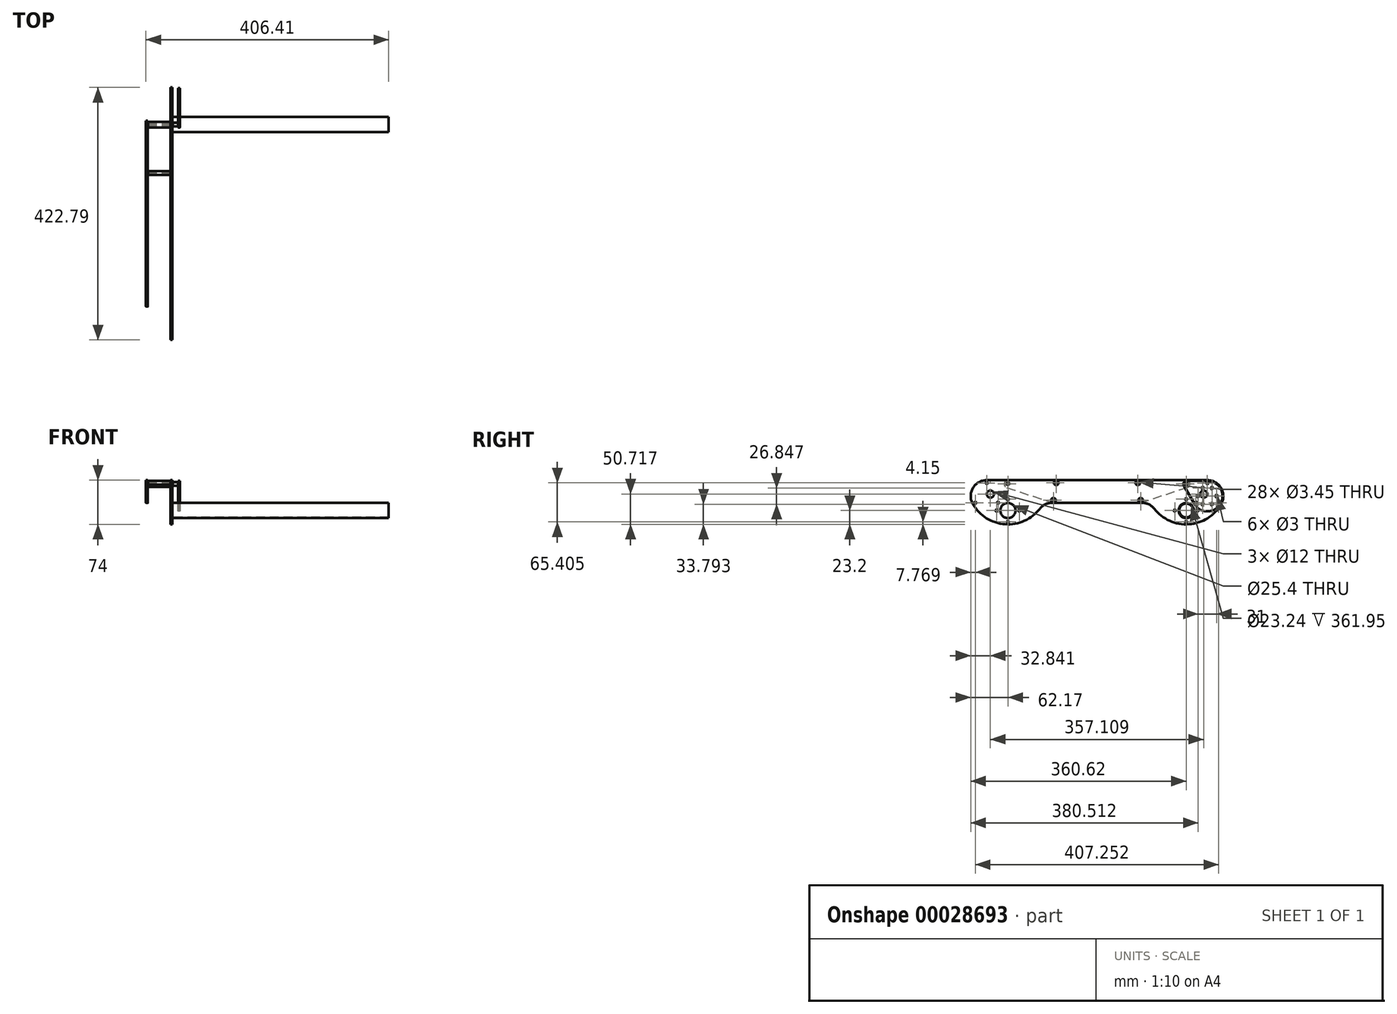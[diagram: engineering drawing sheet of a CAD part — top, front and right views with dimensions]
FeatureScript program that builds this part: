
annotation { "Feature Type Name" : "Feature", "Feature Type Description" : "" }
export const myFeature = defineFeature(function(context is Context, id is Id, definition is map)
    precondition{}
    {
        {
            var Q0;
            Q0=qCreatedBy(makeId("Right.planeOp"),FACE);
            var sketch = newSketch(context, id + "F0", { "sketchPlane" : qUnion([Q0])});
            skCircle(sketch, "E0", {"center": v(0, 0) * mm, "radius": 76.2 * mm});
            skLineSegment(sketch, "E1", {"start": v(79.37, -76.2) * mm, "end": v(-377.83, -76.2) * mm, "construction": true});
            skLineSegment(sketch, "E2", {"start": v(-229.18, -31.75) * mm, "end": v(-69.27, -31.75) * mm});
            skCircle(sketch, "E3.cCircle", {"center": v(-94.33, -49.53) * mm, "radius": 6.35 * mm, "construction": true});
            skLineSegment(sketch, "E3.0", {"start": v(-90.67, -43.18) * mm, "end": v(-87, -49.53) * mm});
            skLineSegment(sketch, "E3.1", {"start": v(-87, -49.53) * mm, "end": v(-90.67, -55.88) * mm});
            skLineSegment(sketch, "E3.2", {"start": v(-90.67, -55.88) * mm, "end": v(-98, -55.88) * mm});
            skLineSegment(sketch, "E3.3", {"start": v(-98, -55.88) * mm, "end": v(-101.67, -49.53) * mm});
            skLineSegment(sketch, "E3.4", {"start": v(-101.67, -49.53) * mm, "end": v(-98, -43.18) * mm});
            skLineSegment(sketch, "E3.5", {"start": v(-98, -43.18) * mm, "end": v(-90.67, -43.18) * mm});
            skPoint(sketch, "E3.0.midPoint", {"position": v(-88.84, -46.35) * mm});
            skLineSegment(sketch, "E4", {"start": v(79.37, -76.2) * mm, "end": v(79.37, 381) * mm, "construction": true});
            skLineSegment(sketch, "E5", {"start": v(79.38, 381) * mm, "end": v(-377.83, 381) * mm, "construction": true});
            skLineSegment(sketch, "E6", {"start": v(-377.83, 381) * mm, "end": v(-377.83, -76.2) * mm, "construction": true});
            skCircle(sketch, "E7", {"center": v(-298.45, 0) * mm, "radius": 76.2 * mm});
            skLineSegment(sketch, "E8", {"start": v(-149.23, -76.2) * mm, "end": v(-149.23, 381) * mm, "construction": true});
            skLineSegment(sketch, "E9", {"start": v(-75.93, 6.35) * mm, "end": v(-222.52, 6.35) * mm});
            skCircle(sketch, "E10", {"center": v(0, 0) * mm, "radius": 50.8 * mm, "construction": true});
            skCircle(sketch, "E11", {"center": v(29.33, -16.93) * mm, "radius": 16.93 * mm, "construction": true});
            skLineSegment(sketch, "E12", {"start": v(0, 0) * mm, "end": v(0, -50.8) * mm, "construction": true});
            skLineSegment(sketch, "E13", {"start": v(0, 0) * mm, "end": v(29.33, -16.93) * mm, "construction": true});
            skCircle(sketch, "E14", {"center": v(0, 0) * mm, "radius": 4.76 * mm, "construction": true});
            skCircle(sketch, "E15", {"center": v(0, -44.45) * mm, "radius": 12.7 * mm});
            skLineSegment(sketch, "E16.rect.bottom", {"start": v(-2.03, -65.53) * mm, "end": v(-21.08, -46.48) * mm});
            skLineSegment(sketch, "E16.rect.top", {"start": v(21.08, -42.42) * mm, "end": v(2.03, -23.37) * mm});
            skLineSegment(sketch, "E16.rect.left", {"start": v(2.03, -65.53) * mm, "end": v(21.08, -46.48) * mm});
            skLineSegment(sketch, "E16.rect.right", {"start": v(-21.08, -42.42) * mm, "end": v(-2.03, -23.37) * mm});
            skPoint(sketch, "E17.visualSharp", {"position": v(23.1, -44.45) * mm});
            skArc(sketch, "E17.filletArc", {"start": v(21.08, -46.48) * mm, "mid": v(21.92, -44.45) * mm, "end": v(21.08, -42.42) * mm});
            skPoint(sketch, "E18.visualSharp", {"position": v(0, -67.56) * mm});
            skArc(sketch, "E18.filletArc", {"start": v(-2.03, -65.53) * mm, "mid": v(0, -66.37) * mm, "end": v(2.03, -65.53) * mm});
            skPoint(sketch, "E19.visualSharp", {"position": v(-23.1, -44.45) * mm});
            skArc(sketch, "E19.filletArc", {"start": v(-21.08, -42.42) * mm, "mid": v(-21.92, -44.45) * mm, "end": v(-21.08, -46.48) * mm});
            skPoint(sketch, "E20.visualSharp", {"position": v(0, -21.34) * mm});
            skArc(sketch, "E20.filletArc", {"start": v(2.03, -23.37) * mm, "mid": v(0, -22.53) * mm, "end": v(-2.03, -23.37) * mm});
            skLineSegment(sketch, "E21", {"start": v(0, 0) * mm, "end": v(0, -44.45) * mm});
            skCircle(sketch, "E22.MirrorC", {"center": v(-298.45, -44.45) * mm, "radius": 12.7 * mm});
            skArc(sketch, "E23.MirrorCS", {"start": v(-300.48, -23.37) * mm, "mid": v(-298.45, -22.53) * mm, "end": v(-296.42, -23.37) * mm});
            skArc(sketch, "E24.MirrorCS", {"start": v(-319.53, -46.48) * mm, "mid": v(-320.37, -44.45) * mm, "end": v(-319.53, -42.42) * mm});
            skLineSegment(sketch, "E25.MirrorCS", {"start": v(-319.53, -42.42) * mm, "end": v(-300.48, -23.37) * mm});
            skLineSegment(sketch, "E26.MirrorCS", {"start": v(-300.48, -65.53) * mm, "end": v(-319.53, -46.48) * mm});
            skArc(sketch, "E27.MirrorCS", {"start": v(-296.42, -65.53) * mm, "mid": v(-298.45, -66.37) * mm, "end": v(-300.48, -65.53) * mm});
            skLineSegment(sketch, "E28.MirrorCS", {"start": v(-277.37, -42.42) * mm, "end": v(-296.42, -23.37) * mm});
            skLineSegment(sketch, "E29.MirrorCS", {"start": v(-296.42, -65.53) * mm, "end": v(-277.37, -46.48) * mm});
            skArc(sketch, "E30.MirrorCS", {"start": v(-277.37, -42.42) * mm, "mid": v(-276.53, -44.45) * mm, "end": v(-277.37, -46.48) * mm});
            skCircle(sketch, "E31", {"center": v(0, -44.45) * mm, "radius": 19.05 * mm});
            skCircle(sketch, "E32", {"center": v(0, -44.45) * mm, "radius": 11.62 * mm});
            skCircle(sketch, "E33", {"center": v(0, -44.45) * mm, "radius": 26.92 * mm, "construction": true});
            skSolve(sketch);
        }
        {
            var Q0;
            Q0=qCreatedBy(makeId("Right.planeOp"),FACE);
            var sketch = newSketch(context, id + "F1", { "sketchPlane" : qUnion([Q0])});
            skArc(sketch, "E34", {"start": v(-59.74, -31.75) * mm, "mid": v(-1.19, -67.64) * mm, "end": v(58.59, -33.83) * mm});
            skArc(sketch, "E35", {"start": v(-357.04, -33.83) * mm, "mid": v(-297.26, -67.64) * mm, "end": v(-238.71, -31.75) * mm});
            skLineSegment(sketch, "E36", {"start": v(-333.84, 6.35) * mm, "end": v(35.4, 6.35) * mm});
            skLineSegment(sketch, "E37", {"start": v(-59.74, -31.75) * mm, "end": v(-238.71, -31.75) * mm});
            skCircle(sketch, "E38", {"center": v(0, 0) * mm, "radius": 1.73 * mm});
            skCircle(sketch, "E39", {"center": v(-298.45, 0) * mm, "radius": 1.73 * mm});
            skCircle(sketch, "E40", {"center": v(29.33, -16.93) * mm, "radius": 6 * mm});
            skCircle(sketch, "E41.MirrorC", {"center": v(-327.78, -16.93) * mm, "radius": 6 * mm});
            skArc(sketch, "E42", {"start": v(58.59, -33.82) * mm, "mid": v(58.59, -7.04) * mm, "end": v(35.4, 6.35) * mm});
            skPoint(sketch, "E43.orphan", {"position": v(67.35, 6.35) * mm});
            skArc(sketch, "E44.MirrorCS", {"start": v(-357.04, -33.83) * mm, "mid": v(-357.04, -7.04) * mm, "end": v(-333.84, 6.35) * mm});
            skPoint(sketch, "E45.orphan", {"position": v(-365.8, 6.35) * mm});
            skCircle(sketch, "E46.0", {"center": v(-298.45, -44.45) * mm, "radius": 12.7 * mm});
            skCircle(sketch, "E46.1", {"center": v(0, -44.45) * mm, "radius": 12.7 * mm});
            skSolve(sketch);
        }
        {
            var Q0;
            Q0 = qSketchRegion(id + "F1", true);
            var Q1;
            Q1=makeQuery(id+"F1.imprint","IMPRINT",FACE,{"disambiguationData":[TD([[makeQuery(id+"F1.imprint","IMPRINT",EDGE,{"derivedFrom":sQuery(id+"F1.wireOp",EDGE,"E46.0")}),-1.0]])]});
            var Q2;
            Q2=makeQuery(id+"F1.imprint","IMPRINT",FACE,{"disambiguationData":[TD([[makeQuery(id+"F1.imprint","IMPRINT",EDGE,{"derivedFrom":sQuery(id+"F1.wireOp",EDGE,"E46.1")}),1.0]])]});
            extrude(context, id + "F2", {"entities" : qUnion([Q0, Q1, Q2]), "depth" : 3.17 * mm});
        }
        {
            var Q0;
            Q0=makeQuery(id+"F2.opExtrude","CAP_FACE",FACE,{"disambiguationData":[OSD([sQuery(id+"F1.wireOp",EDGE,"E34"),sQuery(id+"F1.wireOp",EDGE,"E35"),sQuery(id+"F1.wireOp",EDGE,"E36"),sQuery(id+"F1.wireOp",EDGE,"E37"),sQuery(id+"F1.wireOp",EDGE,"E38"),sQuery(id+"F1.wireOp",EDGE,"E39"),sQuery(id+"F1.wireOp",EDGE,"E40"),sQuery(id+"F1.wireOp",EDGE,"E41.MirrorC")])],"isStart":false});
            cPlane(context, id + "F3", {"entities" : qUnion([Q0]), "cplaneType" : CPlaneType.OFFSET, "offset" : 9.52 * mm, "width" : 152.4 * mm, "height" : 152.4 * mm});
        }
        {
            var Q0;
            Q0=qCreatedBy(id+"F3.planeOp",FACE);
            var sketch = newSketch(context, id + "F4", { "sketchPlane" : qUnion([Q0])});
            skCircle(sketch, "E47.0", {"center": v(29.33, -16.93) * mm, "radius": 6 * mm});
            skCircle(sketch, "E48", {"center": v(35.4, -20.43) * mm, "radius": 18.5 * mm, "construction": true});
            skCircle(sketch, "E49.cCircle", {"center": v(35.4, -20.43) * mm, "radius": 15.5 * mm, "construction": true});
            skLineSegment(sketch, "E49.0", {"start": v(27.64, -33.86) * mm, "end": v(19.9, -20.43) * mm, "construction": true});
            skLineSegment(sketch, "E49.1", {"start": v(19.9, -20.43) * mm, "end": v(27.64, -7) * mm, "construction": true});
            skLineSegment(sketch, "E49.2", {"start": v(27.64, -7) * mm, "end": v(43.14, -7) * mm, "construction": true});
            skLineSegment(sketch, "E49.3", {"start": v(43.14, -7) * mm, "end": v(50.9, -20.43) * mm, "construction": true});
            skLineSegment(sketch, "E49.4", {"start": v(50.9, -20.43) * mm, "end": v(43.14, -33.86) * mm, "construction": true});
            skLineSegment(sketch, "E49.5", {"start": v(43.14, -33.86) * mm, "end": v(27.64, -33.86) * mm, "construction": true});
            skArc(sketch, "E50.0", {"start": v(-0.03, 4.76) * mm, "mid": v(-4.12, 2.38) * mm, "end": v(-4.14, -2.36) * mm});
            skArc(sketch, "E51", {"start": v(13.32, -33) * mm, "mid": v(57.39, -33.13) * mm, "end": v(35.24, 4.97) * mm});
            skLineSegment(sketch, "E52", {"start": v(-0.03, 4.76) * mm, "end": v(35.24, 4.97) * mm});
            skLineSegment(sketch, "E53", {"start": v(13.32, -33) * mm, "end": v(-4.14, -2.36) * mm});
            skCircle(sketch, "E54.cCircle", {"center": v(35.4, -20.43) * mm, "radius": 21.95 * mm, "construction": true});
            skLineSegment(sketch, "E54.0", {"start": v(35.4, 1.52) * mm, "end": v(54.4, -31.4) * mm, "construction": true});
            skLineSegment(sketch, "E54.1", {"start": v(54.4, -31.4) * mm, "end": v(16.38, -31.4) * mm, "construction": true});
            skLineSegment(sketch, "E54.2", {"start": v(16.38, -31.4) * mm, "end": v(35.4, 1.52) * mm, "construction": true});
            skCircle(sketch, "E55", {"center": v(54.4, -31.4) * mm, "radius": 2.87 * mm, "construction": true});
            skLineSegment(sketch, "E56", {"start": v(51.41, -29.68) * mm, "end": v(57.39, -33.13) * mm, "construction": true});
            skCircle(sketch, "E57.0", {"center": v(0, 0) * mm, "radius": 1.73 * mm});
            skCircle(sketch, "E58", {"center": v(35.4, 1.52) * mm, "radius": 1.73 * mm});
            skCircle(sketch, "E59", {"center": v(16.38, -31.4) * mm, "radius": 1.73 * mm});
            skCircle(sketch, "E60", {"center": v(54.4, -31.4) * mm, "radius": 1.73 * mm});
            skCircle(sketch, "E61.MirrorC", {"center": v(-352.85, -31.4) * mm, "radius": 1.73 * mm, "construction": true});
            skCircle(sketch, "E62.MirrorC", {"center": v(-333.84, 1.52) * mm, "radius": 1.73 * mm, "construction": true});
            skCircle(sketch, "E63.MirrorC", {"center": v(-314.83, -31.4) * mm, "radius": 1.73 * mm, "construction": true});
            skSolve(sketch);
        }
        {
            var Q0;
            Q0 = qSketchRegion(id + "F4", true);
            extrude(context, id + "F5", {"entities" : qUnion([Q0]), "depth" : 3.17 * mm});
        }
        {
            var Q0;
            Q0=sQuery(id+"F4.wireOp",VERTEX,"E49.2.start");
            var Q1;
            Q1=sQuery(id+"F4.wireOp",VERTEX,"E49.1.start");
            var Q2;
            Q2=sQuery(id+"F4.wireOp",VERTEX,"E49.5.end");
            var Q3;
            Q3=sQuery(id+"F4.wireOp",VERTEX,"E49.5.start");
            var Q4;
            Q4=sQuery(id+"F4.wireOp",VERTEX,"E49.4.start");
            var Q5;
            Q5=sQuery(id+"F4.wireOp",VERTEX,"E49.3.start");
            var Q6;
            Q6=makeQuery(id+"F5.opExtrude","SWEPT_BODY",BODY,{"disambiguationData":[OSD([sQuery(id+"F4.wireOp",EDGE,"E47.0"),sQuery(id+"F4.wireOp",EDGE,"E50.0"),sQuery(id+"F4.wireOp",EDGE,"E51"),sQuery(id+"F4.wireOp",EDGE,"E52"),sQuery(id+"F4.wireOp",EDGE,"E53"),sQuery(id+"F4.wireOp",EDGE,"E57.0"),sQuery(id+"F4.wireOp",EDGE,"E58"),sQuery(id+"F4.wireOp",EDGE,"E59"),sQuery(id+"F4.wireOp",EDGE,"E60")])]});
            hole(context, id + "F6", {"style" : HoleStyle.C_SINK, "holeDiameter" : 3 * mm, "cSinkDiameter" : 6 * mm, "endStyle" : HoleEndStyle.THROUGH, "oppositeDirection" : true, "locations" : qUnion([Q0, Q1, Q2, Q3, Q4, Q5]), "scope" : qUnion([Q6]), "cSinkAngle" : 90 * degree});
        }
        {
            var Q0;
            Q0=sQuery(id+"F4.wireOp",VERTEX,"E54.0.end");
            var Q1;
            Q1=sQuery(id+"F4.wireOp",VERTEX,"E54.2.start");
            var Q2;
            Q2=sQuery(id+"F4.wireOp",VERTEX,"E54.2.end");
            var Q3;
            Q3=sQuery(id+"F4.wireOp",VERTEX,"E62.MirrorC.center");
            var Q4;
            Q4=sQuery(id+"F4.wireOp",VERTEX,"E63.MirrorC.center");
            var Q5;
            Q5=sQuery(id+"F4.wireOp",VERTEX,"E61.MirrorC.center");
            var Q6;
            Q6=makeQuery(id+"F2.opExtrude","SWEPT_BODY",BODY,{"disambiguationData":[OSD([sQuery(id+"F1.wireOp",EDGE,"E34"),sQuery(id+"F1.wireOp",EDGE,"E35"),sQuery(id+"F1.wireOp",EDGE,"E36"),sQuery(id+"F1.wireOp",EDGE,"E37"),sQuery(id+"F1.wireOp",EDGE,"E38"),sQuery(id+"F1.wireOp",EDGE,"E39"),sQuery(id+"F1.wireOp",EDGE,"E40"),sQuery(id+"F1.wireOp",EDGE,"E41.MirrorC")])]});
            hole(context, id + "F7", {"style" : HoleStyle.SIMPLE, "holeDiameter" : 3.45 * mm, "endStyle" : HoleEndStyle.THROUGH, "locations" : qUnion([Q0, Q1, Q2, Q3, Q4, Q5]), "scope" : qUnion([Q6])});
        }
        {
            var Q0;
            Q0=sQuery(id+"F0.wireOp",VERTEX,"E20.filletArc.center");
            var Q1;
            Q1=sQuery(id+"F0.wireOp",VERTEX,"E17.filletArc.center");
            var Q2;
            Q2=sQuery(id+"F0.wireOp",VERTEX,"E18.filletArc.center");
            var Q3;
            Q3=sQuery(id+"F0.wireOp",VERTEX,"E19.filletArc.center");
            var Q4;
            Q4=sQuery(id+"F0.wireOp",VERTEX,"E23.MirrorCS.center");
            var Q5;
            Q5=sQuery(id+"F0.wireOp",VERTEX,"E30.MirrorCS.center");
            var Q6;
            Q6=sQuery(id+"F0.wireOp",VERTEX,"E27.MirrorCS.center");
            var Q7;
            Q7=sQuery(id+"F0.wireOp",VERTEX,"E24.MirrorCS.center");
            var Q8;
            Q8=makeQuery(id+"F2.opExtrude","SWEPT_BODY",BODY,{"disambiguationData":[OSD([sQuery(id+"F1.wireOp",EDGE,"E34"),sQuery(id+"F1.wireOp",EDGE,"E35"),sQuery(id+"F1.wireOp",EDGE,"E36"),sQuery(id+"F1.wireOp",EDGE,"E37"),sQuery(id+"F1.wireOp",EDGE,"E38"),sQuery(id+"F1.wireOp",EDGE,"E39"),sQuery(id+"F1.wireOp",EDGE,"E40"),sQuery(id+"F1.wireOp",EDGE,"E41.MirrorC")])]});
            hole(context, id + "F8", {"style" : HoleStyle.SIMPLE, "holeDiameter" : 3.45 * mm, "endStyle" : HoleEndStyle.THROUGH, "oppositeDirection" : true, "locations" : qUnion([Q0, Q1, Q2, Q3, Q4, Q5, Q6, Q7]), "scope" : qUnion([Q8])});
        }
        {
            var Q0;
            Q0=makeQuery(id+"F2.opExtrude","SWEPT_EDGE",EDGE,{"disambiguationData":[OSD([sQuery(id+"F1.wireOp",EDGE,"E35"),sQuery(id+"F1.wireOp",EDGE,"E37")])]});
            var Q1;
            Q1=makeQuery(id+"F2.opExtrude","SWEPT_EDGE",EDGE,{"disambiguationData":[OSD([sQuery(id+"F1.wireOp",EDGE,"E34"),sQuery(id+"F1.wireOp",EDGE,"E37")])]});
            fillet(context, id + "F9", {"entities" : qUnion([Q0, Q1]), "radius" : 25.4 * mm, "tangentPropagation" : true, "allowEdgeOverflow" : false});
        }
        {
            var Q0;
            Q0=makeQuery(id+"F2.opExtrude","CAP_FACE",FACE,{"disambiguationData":[OSD([sQuery(id+"F1.wireOp",EDGE,"E34"),sQuery(id+"F1.wireOp",EDGE,"E35"),sQuery(id+"F1.wireOp",EDGE,"E36"),sQuery(id+"F1.wireOp",EDGE,"E37"),sQuery(id+"F1.wireOp",EDGE,"E38"),sQuery(id+"F1.wireOp",EDGE,"E39"),sQuery(id+"F1.wireOp",EDGE,"E40"),sQuery(id+"F1.wireOp",EDGE,"E41.MirrorC"),sQuery(id+"F1.wireOp",EDGE,"E42"),sQuery(id+"F1.wireOp",EDGE,"E44.MirrorCS"),sQuery(id+"F1.wireOp",EDGE,"E46.0"),sQuery(id+"F1.wireOp",EDGE,"E46.1")])],"isStart":false});
            var sketch = newSketch(context, id + "F10", { "sketchPlane" : qUnion([Q0])});
            skCircle(sketch, "E64", {"center": v(0, 0) * mm, "radius": 80.96 * mm, "construction": true});
            skCircle(sketch, "E65", {"center": v(-80.94, 1.9) * mm, "radius": 4.45 * mm, "construction": true});
            skCircle(sketch, "E66", {"center": v(-80.94, 1.9) * mm, "radius": 1.7 * mm});
            skCircle(sketch, "E67", {"center": v(-76.22, -27.3) * mm, "radius": 4.45 * mm, "construction": true});
            skCircle(sketch, "E68", {"center": v(-76.22, -27.3) * mm, "radius": 1.7 * mm});
            skCircle(sketch, "E69.MirrorC", {"center": v(-217.5, 1.9) * mm, "radius": 1.7 * mm});
            skCircle(sketch, "E70.MirrorC", {"center": v(-222.23, -27.3) * mm, "radius": 1.7 * mm});
            skSolve(sketch);
        }
        {
            var Q0;
            Q0=makeQuery(id+"F1.imprint","IMPRINT",FACE,{"disambiguationData":[TD([[makeQuery(id+"F1.imprint","IMPRINT",EDGE,{"derivedFrom":sQuery(id+"F1.wireOp",EDGE,"E34")}),1.0]])]});
            cPlane(context, id + "F11", {"entities" : qUnion([Q0]), "cplaneType" : CPlaneType.OFFSET, "offset" : 38.1 * mm, "oppositeDirection" : true, "width" : 152.4 * mm, "height" : 152.4 * mm});
        }
        {
            var Q0;
            Q0=qCreatedBy(id+"F11.planeOp",FACE);
            var sketch = newSketch(context, id + "F12", { "sketchPlane" : qUnion([Q0])});
            skLineSegment(sketch, "E71.0", {"start": v(-298.45, 6.35) * mm, "end": v(0, 6.35) * mm});
            skLineSegment(sketch, "E71.1", {"start": v(-77.55, -31.75) * mm, "end": v(-220.9, -31.75) * mm});
            skArc(sketch, "E72", {"start": v(2, -6.03) * mm, "mid": v(6.27, 1.01) * mm, "end": v(0, 6.35) * mm});
            skArc(sketch, "E73", {"start": v(-298.45, 6.35) * mm, "mid": v(-304.72, 1.01) * mm, "end": v(-300.45, -6.03) * mm});
            skPoint(sketch, "E74.orphan", {"position": v(35.4, 6.35) * mm});
            skPoint(sketch, "E75.orphan", {"position": v(-333.84, 6.35) * mm});
            skLineSegment(sketch, "E76", {"start": v(-300.45, -6.03) * mm, "end": v(-224.9, -31.1) * mm});
            skLineSegment(sketch, "E77", {"start": v(2, -6.03) * mm, "end": v(-73.55, -31.1) * mm});
            skCircle(sketch, "E78.0", {"center": v(0, 0) * mm, "radius": 1.73 * mm});
            skCircle(sketch, "E79.1", {"center": v(-298.45, 0) * mm, "radius": 1.73 * mm});
            skLineSegment(sketch, "E80", {"start": v(-149.23, 6.35) * mm, "end": v(-149.23, -31.75) * mm, "construction": true});
            skPoint(sketch, "E81.visualSharp", {"position": v(-75.5, -31.75) * mm});
            skArc(sketch, "E81.filletArc", {"start": v(-77.55, -31.75) * mm, "mid": v(-75.53, -31.59) * mm, "end": v(-73.55, -31.1) * mm});
            skPoint(sketch, "E82.visualSharp", {"position": v(-222.95, -31.75) * mm});
            skArc(sketch, "E82.filletArc", {"start": v(-224.9, -31.1) * mm, "mid": v(-222.92, -31.59) * mm, "end": v(-220.9, -31.75) * mm});
            skSolve(sketch);
        }
        {
            var Q0;
            Q0 = qSketchRegion(id + "F12", true);
            extrude(context, id + "F13", {"entities" : qUnion([Q0]), "oppositeDirection" : true, "depth" : 3.17 * mm});
        }
        {
            var Q0;
            Q0=makeQuery(id+"F2.opExtrude","CAP_FACE",FACE,{"disambiguationData":[OSD([sQuery(id+"F1.wireOp",EDGE,"E34"),sQuery(id+"F1.wireOp",EDGE,"E35"),sQuery(id+"F1.wireOp",EDGE,"E36"),sQuery(id+"F1.wireOp",EDGE,"E37"),sQuery(id+"F1.wireOp",EDGE,"E38"),sQuery(id+"F1.wireOp",EDGE,"E39"),sQuery(id+"F1.wireOp",EDGE,"E40"),sQuery(id+"F1.wireOp",EDGE,"E41.MirrorC"),sQuery(id+"F1.wireOp",EDGE,"E42"),sQuery(id+"F1.wireOp",EDGE,"E44.MirrorCS")])],"isStart":true});
            var sketch = newSketch(context, id + "F14", { "sketchPlane" : qUnion([Q0])});
            skCircle(sketch, "E83", {"center": v(0, 0) * mm, "radius": 4.76 * mm});
            skCircle(sketch, "E84", {"center": v(0, 0) * mm, "radius": 1.35 * mm});
            skSolve(sketch);
        }
        {
            var Q0;
            Q0 = qSketchRegion(id + "F14", true);
            var Q1;
            Q1=makeQuery(id+"F13.opExtrude","CAP_FACE",FACE,{"disambiguationData":[OSD([sQuery(id+"F12.wireOp",EDGE,"E71.0"),sQuery(id+"F12.wireOp",EDGE,"E71.1"),sQuery(id+"F12.wireOp",EDGE,"E72"),sQuery(id+"F12.wireOp",EDGE,"E73"),sQuery(id+"F12.wireOp",EDGE,"E76"),sQuery(id+"F12.wireOp",EDGE,"E77"),sQuery(id+"F12.wireOp",EDGE,"E78.0"),sQuery(id+"F12.wireOp",EDGE,"E79.1")])],"isStart":true});
            extrude(context, id + "F15", {"entities" : qUnion([Q0]), "endBound" : BoundingType.UP_TO_SURFACE, "endBoundEntityFace" : qUnion([Q1]), "depth" : 25.4 * mm});
        }
        {
            var Q0;
            Q0=makeQuery(id+"F15.opExtrude","SWEPT_FACE",FACE,{"disambiguationData":[OSD([sQuery(id+"F14.wireOp",EDGE,"E83")])]});
            var Q1;
            Q1=makeQuery(id+"F15.opExtrude","SWEPT_FACE",FACE,{"disambiguationData":[OSD([sQuery(id+"F14.wireOp",EDGE,"E84")])]});
            chamfer(context, id + "F16", {"entities" : qUnion([Q0, Q1]), "width" : 0.25 * mm, "tangentPropagation" : true});
        }
        {
            var Q0;
            Q0=sQuery(id+"F10.wireOp",VERTEX,"E66.center");
            var Q1;
            Q1=sQuery(id+"F10.wireOp",VERTEX,"E68.center");
            var Q2;
            Q2=sQuery(id+"F10.wireOp",VERTEX,"E69.MirrorC.center");
            var Q3;
            Q3=sQuery(id+"F10.wireOp",VERTEX,"E70.MirrorC.center");
            var Q4;
            Q4=makeQuery(id+"F2.opExtrude","SWEPT_BODY",BODY,{"disambiguationData":[OSD([sQuery(id+"F1.wireOp",EDGE,"E34"),sQuery(id+"F1.wireOp",EDGE,"E35"),sQuery(id+"F1.wireOp",EDGE,"E36"),sQuery(id+"F1.wireOp",EDGE,"E37"),sQuery(id+"F1.wireOp",EDGE,"E38"),sQuery(id+"F1.wireOp",EDGE,"E39"),sQuery(id+"F1.wireOp",EDGE,"E40"),sQuery(id+"F1.wireOp",EDGE,"E41.MirrorC"),sQuery(id+"F1.wireOp",EDGE,"E42"),sQuery(id+"F1.wireOp",EDGE,"E44.MirrorCS"),sQuery(id+"F1.wireOp",EDGE,"E46.0"),sQuery(id+"F1.wireOp",EDGE,"E46.1")])]});
            var Q5;
            Q5=makeQuery(id+"F13.opExtrude","SWEPT_BODY",BODY,{"disambiguationData":[OSD([sQuery(id+"F12.wireOp",EDGE,"E71.0"),sQuery(id+"F12.wireOp",EDGE,"E71.1"),sQuery(id+"F12.wireOp",EDGE,"E72"),sQuery(id+"F12.wireOp",EDGE,"E73"),sQuery(id+"F12.wireOp",EDGE,"E76"),sQuery(id+"F12.wireOp",EDGE,"E77"),sQuery(id+"F12.wireOp",EDGE,"E78.0"),sQuery(id+"F12.wireOp",EDGE,"E79.1")])]});
            hole(context, id + "F17", {"style" : HoleStyle.SIMPLE, "holeDiameter" : 3.45 * mm, "endStyle" : HoleEndStyle.THROUGH, "locations" : qUnion([Q0, Q1, Q2, Q3]), "scope" : qUnion([Q4, Q5])});
        }
        {
            var Q0;
            Q0=makeQuery(id+"F5.opExtrude","CAP_FACE",FACE,{"disambiguationData":[OSD([sQuery(id+"F4.wireOp",EDGE,"E47.0"),sQuery(id+"F4.wireOp",EDGE,"E50.0"),sQuery(id+"F4.wireOp",EDGE,"E51"),sQuery(id+"F4.wireOp",EDGE,"E52"),sQuery(id+"F4.wireOp",EDGE,"E53"),sQuery(id+"F4.wireOp",EDGE,"E57.0"),sQuery(id+"F4.wireOp",EDGE,"E58"),sQuery(id+"F4.wireOp",EDGE,"E59"),sQuery(id+"F4.wireOp",EDGE,"E60")])],"isStart":true});
            var sketch = newSketch(context, id + "F18", { "sketchPlane" : qUnion([Q0])});
            skCircle(sketch, "E85", {"center": v(0, 0) * mm, "radius": 3.18 * mm});
            skCircle(sketch, "E86.0", {"center": v(0, 0) * mm, "radius": 1.73 * mm});
            skSolve(sketch);
        }
        {
            var Q0;
            Q0 = qSketchRegion(id + "F18", true);
            var Q1;
            Q1=makeQuery(id+"F2.opExtrude","CAP_FACE",FACE,{"disambiguationData":[OSD([sQuery(id+"F1.wireOp",EDGE,"E34"),sQuery(id+"F1.wireOp",EDGE,"E35"),sQuery(id+"F1.wireOp",EDGE,"E36"),sQuery(id+"F1.wireOp",EDGE,"E37"),sQuery(id+"F1.wireOp",EDGE,"E38"),sQuery(id+"F1.wireOp",EDGE,"E39"),sQuery(id+"F1.wireOp",EDGE,"E40"),sQuery(id+"F1.wireOp",EDGE,"E41.MirrorC"),sQuery(id+"F1.wireOp",EDGE,"E42"),sQuery(id+"F1.wireOp",EDGE,"E44.MirrorCS"),sQuery(id+"F1.wireOp",EDGE,"E46.0"),sQuery(id+"F1.wireOp",EDGE,"E46.1")])],"isStart":false});
            extrude(context, id + "F19", {"entities" : qUnion([Q0]), "endBound" : BoundingType.UP_TO_SURFACE, "endBoundEntityFace" : qUnion([Q1]), "depth" : 25.4 * mm});
        }
        {
            var Q0;
            Q0=makeQuery(id+"F19.opExtrude","SWEPT_FACE",FACE,{"disambiguationData":[OSD([sQuery(id+"F18.wireOp",EDGE,"E85")])]});
            var Q1;
            Q1=makeQuery(id+"F19.opExtrude","SWEPT_FACE",FACE,{"disambiguationData":[OSD([sQuery(id+"F18.wireOp",EDGE,"E86.0")])]});
            chamfer(context, id + "F20", {"entities" : qUnion([Q0, Q1]), "width" : 0.25 * mm, "tangentPropagation" : true});
        }
        {
            var Q0;
            Q0=sQuery(id+"F4.wireOp",VERTEX,"E54.0.start");
            var Q1;
            Q1=sQuery(id+"F4.wireOp",VERTEX,"E54.0.end");
            var Q2;
            Q2=sQuery(id+"F4.wireOp",VERTEX,"E59.center");
            var Q3;
            Q3=makeQuery(id+"F2.opExtrude","SWEPT_BODY",BODY,{"disambiguationData":[OSD([sQuery(id+"F1.wireOp",EDGE,"E34"),sQuery(id+"F1.wireOp",EDGE,"E35"),sQuery(id+"F1.wireOp",EDGE,"E36"),sQuery(id+"F1.wireOp",EDGE,"E37"),sQuery(id+"F1.wireOp",EDGE,"E38"),sQuery(id+"F1.wireOp",EDGE,"E39"),sQuery(id+"F1.wireOp",EDGE,"E40"),sQuery(id+"F1.wireOp",EDGE,"E41.MirrorC"),sQuery(id+"F1.wireOp",EDGE,"E42"),sQuery(id+"F1.wireOp",EDGE,"E44.MirrorCS"),sQuery(id+"F1.wireOp",EDGE,"E46.0"),sQuery(id+"F1.wireOp",EDGE,"E46.1")])]});
            hole(context, id + "F21", {"style" : HoleStyle.SIMPLE, "holeDiameter" : 4.76 * mm, "endStyle" : HoleEndStyle.THROUGH, "locations" : qUnion([Q0, Q1, Q2]), "scope" : qUnion([Q3])});
        }
        {
            var Q0;
            Q0=makeQuery(id+"F2.opExtrude","CAP_FACE",FACE,{"disambiguationData":[OSD([sQuery(id+"F1.wireOp",EDGE,"E34"),sQuery(id+"F1.wireOp",EDGE,"E35"),sQuery(id+"F1.wireOp",EDGE,"E36"),sQuery(id+"F1.wireOp",EDGE,"E37"),sQuery(id+"F1.wireOp",EDGE,"E38"),sQuery(id+"F1.wireOp",EDGE,"E39"),sQuery(id+"F1.wireOp",EDGE,"E40"),sQuery(id+"F1.wireOp",EDGE,"E41.MirrorC"),sQuery(id+"F1.wireOp",EDGE,"E42"),sQuery(id+"F1.wireOp",EDGE,"E44.MirrorCS"),sQuery(id+"F1.wireOp",EDGE,"E46.0"),sQuery(id+"F1.wireOp",EDGE,"E46.1")])],"isStart":true});
            var sketch = newSketch(context, id + "F22", { "sketchPlane" : qUnion([Q0])});
            skCircle(sketch, "E87", {"center": v(80.94, 1.9) * mm, "radius": 3.18 * mm});
            skCircle(sketch, "E88", {"center": v(80.94, 1.9) * mm, "radius": 1.35 * mm});
            skSolve(sketch);
        }
        {
            var Q0;
            Q0 = qSketchRegion(id + "F22", true);
            var Q1;
            Q1=makeQuery(id+"F13.opExtrude","CAP_FACE",FACE,{"disambiguationData":[OSD([sQuery(id+"F12.wireOp",EDGE,"E71.0"),sQuery(id+"F12.wireOp",EDGE,"E71.1"),sQuery(id+"F12.wireOp",EDGE,"E72"),sQuery(id+"F12.wireOp",EDGE,"E73"),sQuery(id+"F12.wireOp",EDGE,"E76"),sQuery(id+"F12.wireOp",EDGE,"E77"),sQuery(id+"F12.wireOp",EDGE,"E78.0"),sQuery(id+"F12.wireOp",EDGE,"E79.1")])],"isStart":true});
            extrude(context, id + "F23", {"entities" : qUnion([Q0]), "endBound" : BoundingType.UP_TO_SURFACE, "endBoundEntityFace" : qUnion([Q1]), "depth" : 25.4 * mm});
        }
        {
            var Q0;
            Q0=makeQuery(id+"F23.opExtrude","SWEPT_FACE",FACE,{"disambiguationData":[OSD([sQuery(id+"F22.wireOp",EDGE,"E87")])]});
            var Q1;
            Q1=makeQuery(id+"F23.opExtrude","SWEPT_FACE",FACE,{"disambiguationData":[OSD([sQuery(id+"F22.wireOp",EDGE,"E88")])]});
            chamfer(context, id + "F24", {"entities" : qUnion([Q0, Q1]), "width" : 0.25 * mm, "tangentPropagation" : true});
        }
        {
            var Q0;
            Q0=makeQuery(id+"F13.opExtrude","CAP_FACE",FACE,{"disambiguationData":[OSD([sQuery(id+"F12.wireOp",EDGE,"E71.0"),sQuery(id+"F12.wireOp",EDGE,"E71.1"),sQuery(id+"F12.wireOp",EDGE,"E72"),sQuery(id+"F12.wireOp",EDGE,"E73"),sQuery(id+"F12.wireOp",EDGE,"E76"),sQuery(id+"F12.wireOp",EDGE,"E77"),sQuery(id+"F12.wireOp",EDGE,"E78.0"),sQuery(id+"F12.wireOp",EDGE,"E79.1"),sQuery(id+"F12.wireOp",EDGE,"E81.filletArc"),sQuery(id+"F12.wireOp",EDGE,"E82.filletArc")])],"isStart":false});
            var sketch = newSketch(context, id + "F25", { "sketchPlane" : qUnion([Q0])});
            skCircle(sketch, "E89.0", {"center": v(298.45, 0) * mm, "radius": 1.73 * mm});
            skCircle(sketch, "E89.1", {"center": v(217.5, 1.9) * mm, "radius": 1.73 * mm});
            skCircle(sketch, "E89.2", {"center": v(222.23, -27.3) * mm, "radius": 1.73 * mm});
            skCircle(sketch, "E89.3", {"center": v(76.22, -27.3) * mm, "radius": 1.73 * mm});
            skCircle(sketch, "E89.4", {"center": v(80.94, 1.9) * mm, "radius": 1.73 * mm});
            skCircle(sketch, "E89.5", {"center": v(0, 0) * mm, "radius": 1.73 * mm});
            skSolve(sketch);
        }
        {
            var Q0;
            Q0=sQuery(id+"F25.wireOp",VERTEX,"E89.5.center");
            var Q1;
            Q1=sQuery(id+"F25.wireOp",VERTEX,"E89.4.center");
            var Q2;
            Q2=sQuery(id+"F25.wireOp",VERTEX,"E89.3.center");
            var Q3;
            Q3=sQuery(id+"F25.wireOp",VERTEX,"E89.1.center");
            var Q4;
            Q4=sQuery(id+"F25.wireOp",VERTEX,"E89.2.center");
            var Q5;
            Q5=sQuery(id+"F25.wireOp",VERTEX,"E89.0.center");
            var Q6;
            Q6=makeQuery(id+"F13.opExtrude","SWEPT_BODY",BODY,{"disambiguationData":[OSD([sQuery(id+"F12.wireOp",EDGE,"E71.0"),sQuery(id+"F12.wireOp",EDGE,"E71.1"),sQuery(id+"F12.wireOp",EDGE,"E72"),sQuery(id+"F12.wireOp",EDGE,"E73"),sQuery(id+"F12.wireOp",EDGE,"E76"),sQuery(id+"F12.wireOp",EDGE,"E77"),sQuery(id+"F12.wireOp",EDGE,"E78.0"),sQuery(id+"F12.wireOp",EDGE,"E79.1"),sQuery(id+"F12.wireOp",EDGE,"E81.filletArc"),sQuery(id+"F12.wireOp",EDGE,"E82.filletArc")])]});
            hole(context, id + "F26", {"style" : HoleStyle.C_SINK, "holeDiameter" : 3.45 * mm, "cSinkDiameter" : 7.8 * mm, "endStyle" : HoleEndStyle.THROUGH, "locations" : qUnion([Q0, Q1, Q2, Q3, Q4, Q5]), "scope" : qUnion([Q6]), "cSinkAngle" : 90 * degree});
        }
        {
            var Q0;
            Q0=makeQuery(id+"F2.opExtrude","CAP_FACE",FACE,{"disambiguationData":[OSD([sQuery(id+"F1.wireOp",EDGE,"E34"),sQuery(id+"F1.wireOp",EDGE,"E35"),sQuery(id+"F1.wireOp",EDGE,"E36"),sQuery(id+"F1.wireOp",EDGE,"E37"),sQuery(id+"F1.wireOp",EDGE,"E38"),sQuery(id+"F1.wireOp",EDGE,"E39"),sQuery(id+"F1.wireOp",EDGE,"E40"),sQuery(id+"F1.wireOp",EDGE,"E41.MirrorC"),sQuery(id+"F1.wireOp",EDGE,"E42"),sQuery(id+"F1.wireOp",EDGE,"E44.MirrorCS"),sQuery(id+"F1.wireOp",EDGE,"E46.0"),sQuery(id+"F1.wireOp",EDGE,"E46.1")])],"isStart":false});
            var sketch = newSketch(context, id + "F27", { "sketchPlane" : qUnion([Q0])});
            skCircle(sketch, "E90.0", {"center": v(-217.5, 1.9) * mm, "radius": 1.73 * mm});
            skCircle(sketch, "E90.1", {"center": v(-222.23, -27.3) * mm, "radius": 1.73 * mm});
            skCircle(sketch, "E90.2", {"center": v(-76.22, -27.3) * mm, "radius": 1.73 * mm});
            skCircle(sketch, "E90.3", {"center": v(-80.94, 1.9) * mm, "radius": 1.73 * mm});
            skSolve(sketch);
        }
        {
            var Q0;
            Q0=sQuery(id+"F27.wireOp",VERTEX,"E90.0.center");
            var Q1;
            Q1=sQuery(id+"F27.wireOp",VERTEX,"E90.1.center");
            var Q2;
            Q2=sQuery(id+"F27.wireOp",VERTEX,"E90.3.center");
            var Q3;
            Q3=sQuery(id+"F27.wireOp",VERTEX,"E90.2.center");
            var Q4;
            Q4=makeQuery(id+"F2.opExtrude","SWEPT_BODY",BODY,{"disambiguationData":[OSD([sQuery(id+"F1.wireOp",EDGE,"E34"),sQuery(id+"F1.wireOp",EDGE,"E35"),sQuery(id+"F1.wireOp",EDGE,"E36"),sQuery(id+"F1.wireOp",EDGE,"E37"),sQuery(id+"F1.wireOp",EDGE,"E38"),sQuery(id+"F1.wireOp",EDGE,"E39"),sQuery(id+"F1.wireOp",EDGE,"E40"),sQuery(id+"F1.wireOp",EDGE,"E41.MirrorC"),sQuery(id+"F1.wireOp",EDGE,"E42"),sQuery(id+"F1.wireOp",EDGE,"E44.MirrorCS"),sQuery(id+"F1.wireOp",EDGE,"E46.0"),sQuery(id+"F1.wireOp",EDGE,"E46.1")])]});
            hole(context, id + "F28", {"style" : HoleStyle.C_SINK, "holeDiameter" : 3.45 * mm, "cSinkDiameter" : 7.8 * mm, "endStyle" : HoleEndStyle.THROUGH, "locations" : qUnion([Q0, Q1, Q2, Q3]), "scope" : qUnion([Q4]), "cSinkAngle" : 90 * degree});
        }
        {
            var Q0;
            Q0=makeQuery(id+"F13.opExtrude","CAP_FACE",FACE,{"disambiguationData":[OSD([sQuery(id+"F12.wireOp",EDGE,"E71.0"),sQuery(id+"F12.wireOp",EDGE,"E71.1"),sQuery(id+"F12.wireOp",EDGE,"E72"),sQuery(id+"F12.wireOp",EDGE,"E73"),sQuery(id+"F12.wireOp",EDGE,"E76"),sQuery(id+"F12.wireOp",EDGE,"E77"),sQuery(id+"F12.wireOp",EDGE,"E78.0"),sQuery(id+"F12.wireOp",EDGE,"E79.1"),sQuery(id+"F12.wireOp",EDGE,"E81.filletArc"),sQuery(id+"F12.wireOp",EDGE,"E82.filletArc")])],"isStart":false});
            cPlane(context, id + "F29", {"entities" : qUnion([Q0]), "cplaneType" : CPlaneType.OFFSET, "offset" : 450.85 * mm, "oppositeDirection" : true, "width" : 152.4 * mm, "height" : 152.4 * mm});
        }
        {
            var Q0;
            Q0=qCreatedBy(id+"F29.planeOp",FACE);
            var Q1;
            Q1=makeQuery(id+"F13.opExtrude","CAP_FACE",FACE,{"disambiguationData":[OSD([sQuery(id+"F12.wireOp",EDGE,"E71.0"),sQuery(id+"F12.wireOp",EDGE,"E71.1"),sQuery(id+"F12.wireOp",EDGE,"E72"),sQuery(id+"F12.wireOp",EDGE,"E73"),sQuery(id+"F12.wireOp",EDGE,"E76"),sQuery(id+"F12.wireOp",EDGE,"E77"),sQuery(id+"F12.wireOp",EDGE,"E78.0"),sQuery(id+"F12.wireOp",EDGE,"E79.1"),sQuery(id+"F12.wireOp",EDGE,"E81.filletArc"),sQuery(id+"F12.wireOp",EDGE,"E82.filletArc")])],"isStart":false});
            cPlane(context, id + "F30", {"entities" : qUnion([Q0, Q1]), "cplaneType" : CPlaneType.MID_PLANE, "offset" : 152.4 * mm, "width" : 152.4 * mm, "height" : 152.4 * mm});
        }
        {
            var Q0;
            Q0=makeQuery(id+"F0.imprint","IMPRINT",FACE,{"disambiguationData":[TD([[makeQuery(id+"F0.imprint","IMPRINT",EDGE,{"derivedFrom":sQuery(id+"F0.wireOp",EDGE,"E15")}),1.0]])]});
            var Q1;
            Q1=qCreatedBy(id+"F30.planeOp",FACE);
            extrude(context, id + "F31", {"entities" : qUnion([Q0]), "endBound" : BoundingType.UP_TO_SURFACE, "endBoundEntityFace" : qUnion([Q1]), "depth" : 25.4 * mm});
        }
        {
            var Q0;
            Q0=makeQuery(id+"F2.opExtrude","SWEPT_BODY",BODY,{"disambiguationData":[OSD([sQuery(id+"F1.wireOp",EDGE,"E34"),sQuery(id+"F1.wireOp",EDGE,"E35"),sQuery(id+"F1.wireOp",EDGE,"E36"),sQuery(id+"F1.wireOp",EDGE,"E37"),sQuery(id+"F1.wireOp",EDGE,"E38"),sQuery(id+"F1.wireOp",EDGE,"E39"),sQuery(id+"F1.wireOp",EDGE,"E40"),sQuery(id+"F1.wireOp",EDGE,"E41.MirrorC"),sQuery(id+"F1.wireOp",EDGE,"E42"),sQuery(id+"F1.wireOp",EDGE,"E44.MirrorCS")])]});
            var Q1;
            Q1=makeQuery(id+"F31.opExtrude","SWEPT_BODY",BODY,{"disambiguationData":[OSD([sQuery(id+"F0.wireOp",EDGE,"E15"),sQuery(id+"F0.wireOp",EDGE,"E32")])]});
            booleanBodies(context, id + "F32", {"operationType" : BooleanOperationType.SUBTRACTION, "tools" : qUnion([Q0]), "targets" : qUnion([Q1]), "keepTools" : true});
        }
        {
            var Q0;
            Q0=makeQuery(id+"F31.opExtrude","SWEPT_BODY",BODY,{"disambiguationData":[OSD([sQuery(id+"F0.wireOp",EDGE,"E15"),sQuery(id+"F0.wireOp",EDGE,"E32")])]});
            var Q1;
            Q1=qCreatedBy(id+"F30.planeOp",FACE);
            mirror(context, id + "F33", {"operationType" : NewBodyOperationType.ADD, "entities" : qUnion([Q0]), "mirrorPlane" : qUnion([Q1])});
        }
    });
